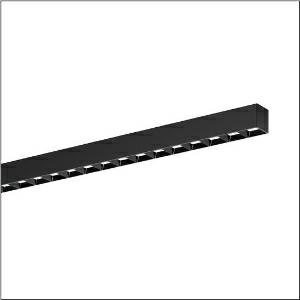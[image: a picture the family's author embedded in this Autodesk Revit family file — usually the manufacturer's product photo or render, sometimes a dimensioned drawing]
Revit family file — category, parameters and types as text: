
# Revit family: silica_r__21_51mx22tat4b_b010
name_source: partatom
category: Lighting Fixtures
units: mm (PartAtom-declared; Revit-internal decimal feet)

## family parameters
Cut with Voids When Loaded = No
Host = Face
Light Source = No
Part Type = Normal
Room Calculation Point = No
Round Connector Dimension = Use Diameter
Shared = No

## types (1)
- --- (1 x LED, 3720 lm, 32.1 W, 6500K)
    Apparent Load = 32 VA
    CIE Flux Codes = 84 100 100 100 100
    Color Rendering = 80
    Color Temperature = 6500K
    Default Elevation = 1800 mm
    Description = Silica® 21, office luminaire, primary light control with darklight reflector, of PMMA, black, CAT 2 (L<= 3000cd/m²), light emission: direct distribution, primary light characteristic: symmetric, installation type: surface-mounted, LED, rated luminous flux: 3.720lm, luminous efficacy: 110lm/W, light colour: 8tw, colour temperature: 2700..6500K, control gear: DALI DT8, with terminal, 3+2-pole, max. 2.5mm², mains connection: 220..240V, AC, 50/60Hz, rated input power: 33.8W, luminaire housing, of aluminium, matt jet black (RAL 9005), length: 1.204mm, width: 53mm, height: 53mm, protection rating (complete): IP20, insulation class (complete): insulation class I (protective earthing), certification: CE, permissible operating ambient temperature: 0..+35°C, standard: EN 50419, packaging unit: 1 piece
    Height = 53 mm
    Lamp = 1 x LED
    Lamp Light Flux = 3720 lm
    Lamp Power = 32.1 W
    Lamp count = 1
    Length = 1204 mm
    Luminous efficacy = 116 lm/W
    Manufacturer = Siteco
    ModVariant = No
    Model = 51MX22TAT4B
    Mounting Place = Ceiling
    Mounting Type = Surface mounted
    Number of Poles = 1
    OnlyDefault = Yes
    Power Factor = 1
    Product Name = Silica® 21
    Product group = office luminaire | ceiling mounted
    ProductGroupID = 302
    Protection Class = Protection class I
    Protection Degree = IP 20
    RLX_Detail_Level = 1
    RLX_Emergency_Light_Flux = 0 lm
    RLX_Emergency_Type = 0
    RLX_Emergency_Type_DB = No
    RlxData = <blob elided: 40249 chars, md5=11c0c358>
    Socket = socket
    Standby Power = 0 W
    System Light Flux = 3720 lm
    System Power = 32 W
    Type Comments = individual setting
    Type Image = l_1335908.jpg
    URL = http://relux.com
    VarID = @adj_140142
    Voltage = 0 V
    Weight = 0.00 kg
    Width = 53 mm

## geometry (parser evidence)
native form markers: Blend x4, Sweep x10
no freeform markers — native parametric forms only
